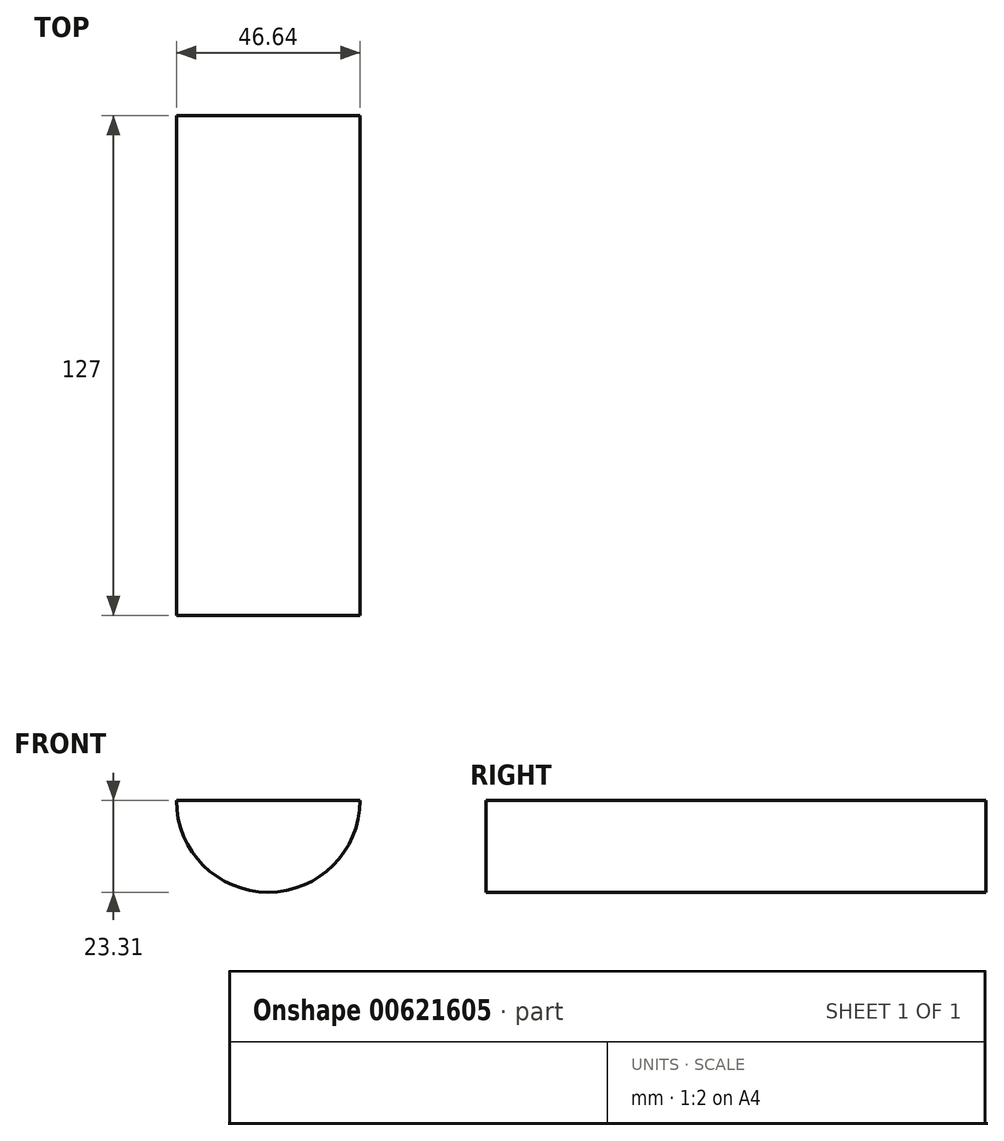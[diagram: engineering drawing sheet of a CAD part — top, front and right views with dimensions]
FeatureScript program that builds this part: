
annotation { "Feature Type Name" : "Feature", "Feature Type Description" : "" }
export const myFeature = defineFeature(function(context is Context, id is Id, definition is map)
    precondition{}
    {
        {
            var Q0;
            Q0=qCreatedBy(makeId("Front.planeOp"),FACE);
            var sketch = newSketch(context, id + "F0", { "sketchPlane" : qUnion([Q0])});
            skArc(sketch, "E0", {"start": v(-17.15, 0) * mm, "mid": v(0, 17.15) * mm, "end": v(17.15, 0) * mm});
            skArc(sketch, "E1", {"start": v(-23.32, -30.2) * mm, "mid": v(0, -53.52) * mm, "end": v(23.32, -30.2) * mm});
            skLineSegment(sketch, "E2", {"start": v(-23.32, -30.2) * mm, "end": v(23.32, -30.2) * mm});
            skLineSegment(sketch, "E3", {"start": v(-17.15, 0) * mm, "end": v(17.15, 0) * mm});
            skSolve(sketch);
        }
        {
            var Q0;
            Q0=makeQuery(id+"F0.imprint","IMPRINT",FACE,{"disambiguationData":[TD([[makeQuery(id+"F0.imprint","IMPRINT",EDGE,{"derivedFrom":sQuery(id+"F0.wireOp",EDGE,"E1")}),1.0]])]});
            var Q1;
            Q1=makeQuery(id+"F0.imprint","IMPRINT",FACE,{"disambiguationData":[TD([[makeQuery(id+"F0.imprint","IMPRINT",EDGE,{"derivedFrom":sQuery(id+"F0.wireOp",EDGE,"E0")}),-1.0]])]});
            extrude(context, id + "F1", {"entities" : qUnion([Q0, Q1]), "depth" : 127 * mm, "offsetDistance" : 25.4 * mm});
        }
    });
